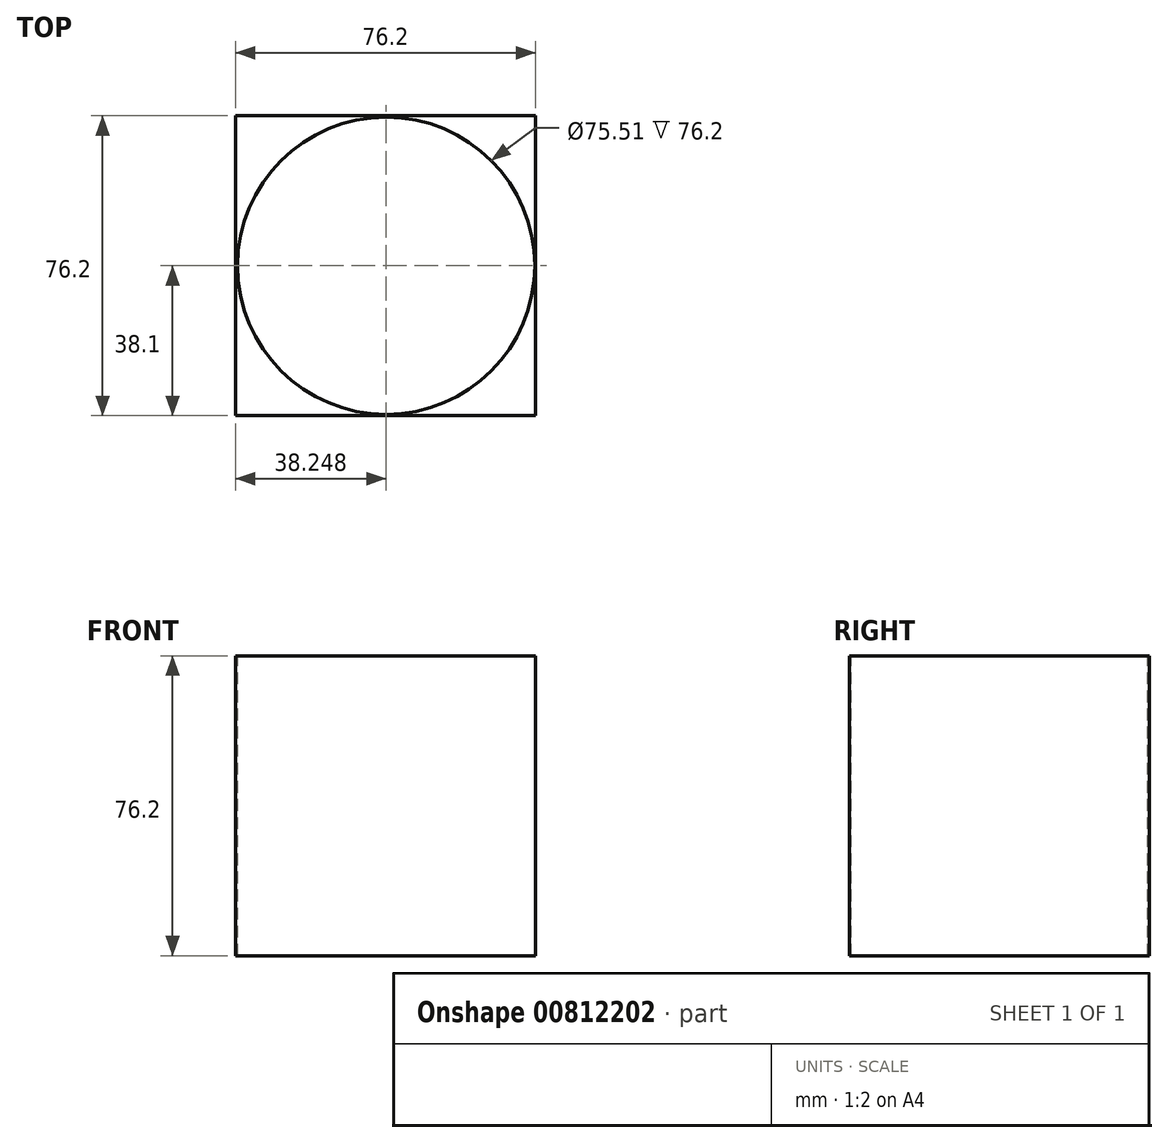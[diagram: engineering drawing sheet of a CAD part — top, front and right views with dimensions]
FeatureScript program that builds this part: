
annotation { "Feature Type Name" : "Feature", "Feature Type Description" : "" }
export const myFeature = defineFeature(function(context is Context, id is Id, definition is map)
    precondition{}
    {
        {
            var Q0;
            Q0=qCreatedBy(makeId("Front.planeOp"),FACE);
            var sketch = newSketch(context, id + "F0", { "sketchPlane" : qUnion([Q0])});
            skLineSegment(sketch, "E0", {"start": v(0, 0) * mm, "end": v(76.2, 0) * mm});
            skLineSegment(sketch, "E1", {"start": v(76.2, 0) * mm, "end": v(76.2, -76.2) * mm});
            skLineSegment(sketch, "E2", {"start": v(76.2, -76.2) * mm, "end": v(0, -76.2) * mm});
            skLineSegment(sketch, "E3", {"start": v(0, -76.2) * mm, "end": v(0, 0) * mm});
            skSolve(sketch);
        }
        {
            var Q0;
            Q0=makeQuery(id+"F0.imprint","IMPRINT",FACE,{"disambiguationData":[TD([[makeQuery(id+"F0.imprint","IMPRINT",EDGE,{"derivedFrom":sQuery(id+"F0.wireOp",EDGE,"E0")}),-1.0]])]});
            extrude(context, id + "F1", {"entities" : qUnion([Q0]), "depth" : 76.2 * mm, "offsetDistance" : 25.4 * mm});
        }
        {
            var Q0;
            Q0=makeQuery(id+"F1.opExtrude","SWEPT_FACE",FACE,{"disambiguationData":[OSD([sQuery(id+"F0.wireOp",EDGE,"E0")])]});
            var sketch = newSketch(context, id + "F2", { "sketchPlane" : qUnion([Q0])});
            skCircle(sketch, "E4", {"center": v(38.25, -38.1) * mm, "radius": 37.76 * mm});
            skPoint(sketch, "E4.centerSnap0", {"position": v(76.2, -38.1) * mm});
            skSolve(sketch);
        }
        {
            var Q0;
            Q0=makeQuery(id+"F2.imprint","IMPRINT",FACE,{"disambiguationData":[TD([[makeQuery(id+"F2.imprint","IMPRINT",EDGE,{"derivedFrom":sQuery(id+"F2.wireOp",EDGE,"E4")}),1.0]])]});
            extrude(context, id + "F3", {"entities" : qUnion([Q0]), "operationType" : NewBodyOperationType.REMOVE, "depth" : -76.2 * mm, "offsetDistance" : 25.4 * mm});
        }
        {
            var Q0;
            Q0=makeQuery(id+"F1.opExtrude","SWEPT_FACE",FACE,{"disambiguationData":[OSD([sQuery(id+"F0.wireOp",EDGE,"E3")])]});
            var sketch = newSketch(context, id + "F4", { "sketchPlane" : qUnion([Q0])});
            skCircle(sketch, "E5", {"center": v(38.98, -37.72) * mm, "radius": 37.7 * mm});
            skCircle(sketch, "E6", {"center": v(38.98, -37.72) * mm, "radius": 37.72 * mm});
            skSolve(sketch);
        }
        {
            var Q0;
            {var subQ0=sQuery(id+"F4.wireOp",EDGE,"E5");var subQ1=makeQuery(id+"F1.opExtrude","CAP_EDGE",EDGE,{"disambiguationData":[OSD([sQuery(id+"F0.wireOp",EDGE,"E3")])],"isStart":false});var subQ2=makeQuery(id+"F4.imprint","INTERSECT",VERTEX,{"disambiguationData":[OD(0.0)],"derivedFrom":[subQ1,subQ0]});Q0=makeQuery(id+"F4.imprint","IMPRINT",FACE,{"disambiguationData":[TD([[makeQuery(id+"F4.imprint","IMPRINT",EDGE,{"disambiguationData":[TD([[subQ2,-1.0]])],"derivedFrom":subQ0}),1.0]])]});}
            extrude(context, id + "F5", {"entities" : qUnion([Q0]), "operationType" : NewBodyOperationType.REMOVE, "oppositeDirection" : true, "depth" : 78.74 * mm, "offsetDistance" : 25.4 * mm});
        }
    });
